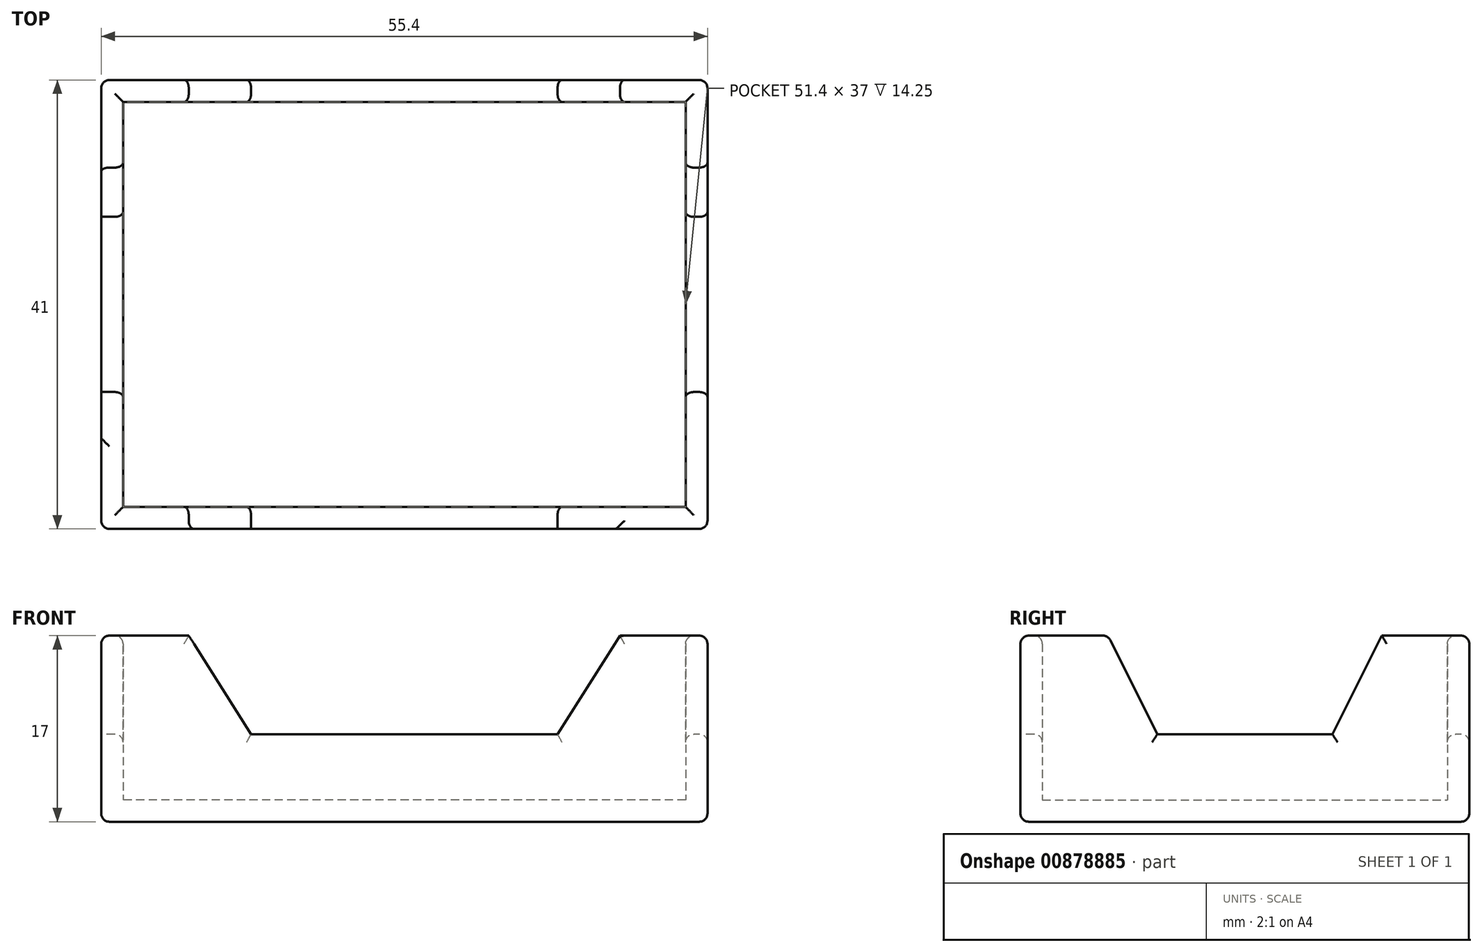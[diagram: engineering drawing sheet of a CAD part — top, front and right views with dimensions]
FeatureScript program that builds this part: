
annotation { "Feature Type Name" : "Feature", "Feature Type Description" : "" }
export const myFeature = defineFeature(function(context is Context, id is Id, definition is map)
    precondition{}
    {
        {
            var Q0;
            Q0=qCreatedBy(makeId("Top.planeOp"),FACE);
            var sketch = newSketch(context, id + "F0", { "sketchPlane" : qUnion([Q0])});
            skLineSegment(sketch, "E0.bottom", {"start": v(25.7, -18.5) * mm, "end": v(-25.7, -18.5) * mm});
            skLineSegment(sketch, "E0.top", {"start": v(25.7, 18.5) * mm, "end": v(-25.7, 18.5) * mm});
            skLineSegment(sketch, "E0.left", {"start": v(25.7, -18.5) * mm, "end": v(25.7, 18.5) * mm});
            skLineSegment(sketch, "E0.right", {"start": v(-25.7, -18.5) * mm, "end": v(-25.7, 18.5) * mm});
            skPoint(sketch, "E0.middle", {"position": v(0, 0) * mm});
            skLineSegment(sketch, "E1.0", {"start": v(27.7, 20.5) * mm, "end": v(-27.7, 20.5) * mm});
            skLineSegment(sketch, "E1.1", {"start": v(27.7, -20.5) * mm, "end": v(27.7, 20.5) * mm});
            skLineSegment(sketch, "E1.2", {"start": v(27.7, -20.5) * mm, "end": v(-27.7, -20.5) * mm});
            skLineSegment(sketch, "E1.3", {"start": v(-27.7, -20.5) * mm, "end": v(-27.7, 20.5) * mm});
            skSolve(sketch);
        }
        {
            var Q0;
            Q0=makeQuery(id+"F0.imprint","IMPRINT",FACE,{"disambiguationData":[TD([[makeQuery(id+"F0.imprint","IMPRINT",EDGE,{"derivedFrom":sQuery(id+"F0.wireOp",EDGE,"E0.bottom")}),1.0]])]});
            extrude(context, id + "F1", {"entities" : qUnion([Q0]), "depth" : 15 * mm, "offsetDistance" : 25 * mm});
        }
        {
            var Q0;
            Q0=makeQuery(id+"F0.imprint","IMPRINT",FACE,{"disambiguationData":[TD([[makeQuery(id+"F0.imprint","IMPRINT",EDGE,{"derivedFrom":sQuery(id+"F0.wireOp",EDGE,"E0.bottom")}),-1.0]])]});
            var Q1;
            Q1=makeQuery(id+"F0.imprint","IMPRINT",FACE,{"disambiguationData":[TD([[makeQuery(id+"F0.imprint","IMPRINT",EDGE,{"derivedFrom":sQuery(id+"F0.wireOp",EDGE,"E0.bottom")}),1.0]])]});
            extrude(context, id + "F2", {"entities" : qUnion([Q0, Q1]), "operationType" : NewBodyOperationType.ADD, "oppositeDirection" : true, "depth" : 2 * mm, "offsetDistance" : 25 * mm});
        }
        {
            var Q0;
            {var subQ0=sQuery(id+"F0.wireOp",EDGE,"E1.2");Q0=makeQuery(id+"F2.boolean.opBoolean","MERGE",FACE,{"derivedFrom":[makeQuery(id+"F1.opExtrude","SWEPT_FACE",FACE,{"disambiguationData":[OSD([subQ0])]}),makeQuery(id+"F2.opExtrude","SWEPT_FACE",FACE,{"disambiguationData":[OSD([subQ0])]})]});}
            var sketch = newSketch(context, id + "F3", { "sketchPlane" : qUnion([Q0])});
            skLineSegment(sketch, "E2", {"start": v(-19.7, 15) * mm, "end": v(-14, 6) * mm});
            skLineSegment(sketch, "E3", {"start": v(-14, 6) * mm, "end": v(14, 6) * mm});
            skLineSegment(sketch, "E4", {"start": v(14, 6) * mm, "end": v(19.7, 15) * mm});
            skSolve(sketch);
        }
        {
            var Q0;
            {var subQ0=sQuery(id+"F3.wireOp",EDGE,"E2");Q0=makeQuery(id+"F3.imprint","IMPRINT",FACE,{"disambiguationData":[TD([[makeQuery(id+"F3.imprint","IMPRINT",EDGE,{"derivedFrom":subQ0}),1.0]])]});}
            extrude(context, id + "F4", {"entities" : qUnion([Q0]), "operationType" : NewBodyOperationType.REMOVE, "endBound" : BoundingType.THROUGH_ALL, "oppositeDirection" : true, "depth" : 25 * mm, "offsetDistance" : 25 * mm});
        }
        {
            var Q0;
            {var subQ0=sQuery(id+"F0.wireOp",EDGE,"E1.3");Q0=makeQuery(id+"F2.boolean.opBoolean","MERGE",FACE,{"derivedFrom":[makeQuery(id+"F1.opExtrude","SWEPT_FACE",FACE,{"disambiguationData":[OSD([subQ0])]}),makeQuery(id+"F2.opExtrude","SWEPT_FACE",FACE,{"disambiguationData":[OSD([subQ0])]})]});}
            var sketch = newSketch(context, id + "F5", { "sketchPlane" : qUnion([Q0])});
            skLineSegment(sketch, "E5", {"start": v(-12.5, 15) * mm, "end": v(-8, 6) * mm});
            skLineSegment(sketch, "E6", {"start": v(-8, 6) * mm, "end": v(8, 6) * mm});
            skLineSegment(sketch, "E7", {"start": v(8, 6) * mm, "end": v(12.5, 15) * mm});
            skSolve(sketch);
        }
        {
            var Q0;
            {var subQ0=sQuery(id+"F5.wireOp",EDGE,"E5");Q0=makeQuery(id+"F5.imprint","IMPRINT",FACE,{"disambiguationData":[TD([[makeQuery(id+"F5.imprint","IMPRINT",EDGE,{"derivedFrom":subQ0}),1.0]])]});}
            extrude(context, id + "F6", {"entities" : qUnion([Q0]), "operationType" : NewBodyOperationType.REMOVE, "endBound" : BoundingType.THROUGH_ALL, "oppositeDirection" : true, "depth" : 25 * mm, "offsetDistance" : 25 * mm});
        }
        {
            var Q0;
            {var subQ0=sQuery(id+"F0.wireOp",EDGE,"E1.0");Q0=makeQuery(id+"F4.boolean.opBoolean","INTERSECT",EDGE,{"derivedFrom":[makeQuery(id+"F2.boolean.opBoolean","MERGE",FACE,{"derivedFrom":[makeQuery(id+"F1.opExtrude","SWEPT_FACE",FACE,{"disambiguationData":[OSD([subQ0])]}),makeQuery(id+"F2.opExtrude","SWEPT_FACE",FACE,{"disambiguationData":[OSD([subQ0])]})]}),makeQuery(id+"F4.opExtrude","SWEPT_FACE",FACE,{"disambiguationData":[OSD([sQuery(id+"F3.wireOp",EDGE,"E3")])]})]});}
            var Q1;
            {var subQ0=sQuery(id+"F0.wireOp",EDGE,"E1.0");Q1=makeQuery(id+"F4.boolean.opBoolean","INTERSECT",EDGE,{"derivedFrom":[makeQuery(id+"F2.boolean.opBoolean","MERGE",FACE,{"derivedFrom":[makeQuery(id+"F1.opExtrude","SWEPT_FACE",FACE,{"disambiguationData":[OSD([subQ0])]}),makeQuery(id+"F2.opExtrude","SWEPT_FACE",FACE,{"disambiguationData":[OSD([subQ0])]})]}),makeQuery(id+"F4.opExtrude","SWEPT_FACE",FACE,{"disambiguationData":[OSD([sQuery(id+"F3.wireOp",EDGE,"E4")])]})]});}
            var Q2;
            {var subQ0=sQuery(id+"F0.wireOp",EDGE,"E1.0");var subQ1=sQuery(id+"F0.wireOp",EDGE,"E1.1");Q2=makeQuery(id+"F4.boolean.opBoolean","SPLIT",EDGE,{"disambiguationData":[TD([makeQuery(id+"F1.opExtrude","SWEPT_FACE",FACE,{"disambiguationData":[OSD([subQ1])]})])],"derivedFrom":makeQuery(id+"F1.opExtrude","CAP_EDGE",EDGE,{"disambiguationData":[OSD([subQ0])],"isStart":false})});}
            var Q3;
            {var subQ0=sQuery(id+"F0.wireOp",EDGE,"E1.0");var subQ1=sQuery(id+"F0.wireOp",EDGE,"E1.1");Q3=makeQuery(id+"F6.boolean.opBoolean","SPLIT",EDGE,{"disambiguationData":[TD([makeQuery(id+"F1.opExtrude","SWEPT_FACE",FACE,{"disambiguationData":[OSD([subQ0])]})])],"derivedFrom":makeQuery(id+"F1.opExtrude","CAP_EDGE",EDGE,{"disambiguationData":[OSD([subQ1])],"isStart":false})});}
            var Q4;
            {var subQ0=sQuery(id+"F0.wireOp",EDGE,"E1.1");var subQ1=sQuery(id+"F0.wireOp",EDGE,"E1.0");Q4=makeQuery(id+"F2.boolean.opBoolean","MERGE",EDGE,{"derivedFrom":[makeQuery(id+"F1.opExtrude","SWEPT_EDGE",EDGE,{"disambiguationData":[OSD([subQ1,subQ0])]}),makeQuery(id+"F2.opExtrude","SWEPT_EDGE",EDGE,{"disambiguationData":[OSD([subQ1,subQ0])]})]});}
            var Q5;
            {var subQ0=sQuery(id+"F0.wireOp",EDGE,"E1.0");Q5=makeQuery(id+"F4.boolean.opBoolean","INTERSECT",EDGE,{"derivedFrom":[makeQuery(id+"F2.boolean.opBoolean","MERGE",FACE,{"derivedFrom":[makeQuery(id+"F1.opExtrude","SWEPT_FACE",FACE,{"disambiguationData":[OSD([subQ0])]}),makeQuery(id+"F2.opExtrude","SWEPT_FACE",FACE,{"disambiguationData":[OSD([subQ0])]})]}),makeQuery(id+"F4.opExtrude","SWEPT_FACE",FACE,{"disambiguationData":[OSD([sQuery(id+"F3.wireOp",EDGE,"E2")])]})]});}
            var Q6;
            {var subQ0=sQuery(id+"F0.wireOp",EDGE,"E1.3");var subQ1=sQuery(id+"F0.wireOp",EDGE,"E1.0");Q6=makeQuery(id+"F4.boolean.opBoolean","SPLIT",EDGE,{"disambiguationData":[TD([makeQuery(id+"F1.opExtrude","SWEPT_FACE",FACE,{"disambiguationData":[OSD([subQ0])]})])],"derivedFrom":makeQuery(id+"F1.opExtrude","CAP_EDGE",EDGE,{"disambiguationData":[OSD([subQ1])],"isStart":false})});}
            var Q7;
            {var subQ0=sQuery(id+"F0.wireOp",EDGE,"E1.3");var subQ1=sQuery(id+"F0.wireOp",EDGE,"E1.0");Q7=makeQuery(id+"F2.boolean.opBoolean","MERGE",EDGE,{"derivedFrom":[makeQuery(id+"F1.opExtrude","SWEPT_EDGE",EDGE,{"disambiguationData":[OSD([subQ1,subQ0])]}),makeQuery(id+"F2.opExtrude","SWEPT_EDGE",EDGE,{"disambiguationData":[OSD([subQ1,subQ0])]})]});}
            var Q8;
            {var subQ0=sQuery(id+"F0.wireOp",EDGE,"E1.3");var subQ1=sQuery(id+"F0.wireOp",EDGE,"E1.0");Q8=makeQuery(id+"F6.boolean.opBoolean","SPLIT",EDGE,{"disambiguationData":[TD([makeQuery(id+"F1.opExtrude","SWEPT_FACE",FACE,{"disambiguationData":[OSD([subQ1])]})])],"derivedFrom":makeQuery(id+"F1.opExtrude","CAP_EDGE",EDGE,{"disambiguationData":[OSD([subQ0])],"isStart":false})});}
            var Q9;
            {var subQ0=sQuery(id+"F0.wireOp",EDGE,"E0.right");var subQ1=sQuery(id+"F0.wireOp",EDGE,"E0.top");Q9=makeQuery(id+"F6.boolean.opBoolean","SPLIT",EDGE,{"disambiguationData":[TD([makeQuery(id+"F1.opExtrude","SWEPT_FACE",FACE,{"disambiguationData":[OSD([subQ1])]})])],"derivedFrom":makeQuery(id+"F1.opExtrude","CAP_EDGE",EDGE,{"disambiguationData":[OSD([subQ0])],"isStart":false})});}
            var Q10;
            {var subQ0=sQuery(id+"F0.wireOp",EDGE,"E0.right");var subQ1=sQuery(id+"F0.wireOp",EDGE,"E0.top");Q10=makeQuery(id+"F4.boolean.opBoolean","SPLIT",EDGE,{"disambiguationData":[TD([makeQuery(id+"F1.opExtrude","SWEPT_FACE",FACE,{"disambiguationData":[OSD([subQ0])]})])],"derivedFrom":makeQuery(id+"F1.opExtrude","CAP_EDGE",EDGE,{"disambiguationData":[OSD([subQ1])],"isStart":false})});}
            var Q11;
            Q11=makeQuery(id+"F4.boolean.opBoolean","INTERSECT",EDGE,{"derivedFrom":[makeQuery(id+"F1.opExtrude","SWEPT_FACE",FACE,{"disambiguationData":[OSD([sQuery(id+"F0.wireOp",EDGE,"E0.top")])]}),makeQuery(id+"F4.opExtrude","SWEPT_FACE",FACE,{"disambiguationData":[OSD([sQuery(id+"F3.wireOp",EDGE,"E2")])]})]});
            var Q12;
            Q12=makeQuery(id+"F4.boolean.opBoolean","INTERSECT",EDGE,{"derivedFrom":[makeQuery(id+"F1.opExtrude","SWEPT_FACE",FACE,{"disambiguationData":[OSD([sQuery(id+"F0.wireOp",EDGE,"E0.top")])]}),makeQuery(id+"F4.opExtrude","SWEPT_FACE",FACE,{"disambiguationData":[OSD([sQuery(id+"F3.wireOp",EDGE,"E3")])]})]});
            var Q13;
            Q13=makeQuery(id+"F4.boolean.opBoolean","INTERSECT",EDGE,{"derivedFrom":[makeQuery(id+"F1.opExtrude","SWEPT_FACE",FACE,{"disambiguationData":[OSD([sQuery(id+"F0.wireOp",EDGE,"E0.top")])]}),makeQuery(id+"F4.opExtrude","SWEPT_FACE",FACE,{"disambiguationData":[OSD([sQuery(id+"F3.wireOp",EDGE,"E4")])]})]});
            var Q14;
            {var subQ0=sQuery(id+"F0.wireOp",EDGE,"E0.left");var subQ1=sQuery(id+"F0.wireOp",EDGE,"E0.top");Q14=makeQuery(id+"F4.boolean.opBoolean","SPLIT",EDGE,{"disambiguationData":[TD([makeQuery(id+"F1.opExtrude","SWEPT_FACE",FACE,{"disambiguationData":[OSD([subQ0])]})])],"derivedFrom":makeQuery(id+"F1.opExtrude","CAP_EDGE",EDGE,{"disambiguationData":[OSD([subQ1])],"isStart":false})});}
            var Q15;
            {var subQ0=sQuery(id+"F0.wireOp",EDGE,"E0.left");var subQ1=sQuery(id+"F0.wireOp",EDGE,"E0.top");Q15=makeQuery(id+"F6.boolean.opBoolean","SPLIT",EDGE,{"disambiguationData":[TD([makeQuery(id+"F1.opExtrude","SWEPT_FACE",FACE,{"disambiguationData":[OSD([subQ1])]})])],"derivedFrom":makeQuery(id+"F1.opExtrude","CAP_EDGE",EDGE,{"disambiguationData":[OSD([subQ0])],"isStart":false})});}
            var Q16;
            {var subQ1=sQuery(id+"F0.wireOp",EDGE,"E0.left");var subQ2=sQuery(id+"F0.wireOp",EDGE,"E1.3");var subQ3=sQuery(id+"F5.wireOp",EDGE,"E5");Q16=makeQuery(id+"F6.boolean.opBoolean","COPY",EDGE,{"disambiguationData":[TD([makeQuery(id+"F1.opExtrude","SWEPT_FACE",FACE,{"disambiguationData":[OSD([subQ1])]})])],"derivedFrom":makeQuery(id+"F6.opExtrude","SWEPT_EDGE",EDGE,{"disambiguationData":[OSD([subQ2,subQ3])]})});}
            var Q17;
            {var subQ0=sQuery(id+"F0.wireOp",EDGE,"E1.1");Q17=makeQuery(id+"F6.boolean.opBoolean","INTERSECT",EDGE,{"derivedFrom":[makeQuery(id+"F2.boolean.opBoolean","MERGE",FACE,{"derivedFrom":[makeQuery(id+"F1.opExtrude","SWEPT_FACE",FACE,{"disambiguationData":[OSD([subQ0])]}),makeQuery(id+"F2.opExtrude","SWEPT_FACE",FACE,{"disambiguationData":[OSD([subQ0])]})]}),makeQuery(id+"F6.opExtrude","SWEPT_FACE",FACE,{"disambiguationData":[OSD([sQuery(id+"F5.wireOp",EDGE,"E5")])]})]});}
            var Q18;
            Q18=makeQuery(id+"F6.boolean.opBoolean","INTERSECT",EDGE,{"derivedFrom":[makeQuery(id+"F1.opExtrude","SWEPT_FACE",FACE,{"disambiguationData":[OSD([sQuery(id+"F0.wireOp",EDGE,"E0.left")])]}),makeQuery(id+"F6.opExtrude","SWEPT_FACE",FACE,{"disambiguationData":[OSD([sQuery(id+"F5.wireOp",EDGE,"E5")])]})]});
            var Q19;
            Q19=makeQuery(id+"F6.boolean.opBoolean","INTERSECT",EDGE,{"derivedFrom":[makeQuery(id+"F1.opExtrude","SWEPT_FACE",FACE,{"disambiguationData":[OSD([sQuery(id+"F0.wireOp",EDGE,"E0.left")])]}),makeQuery(id+"F6.opExtrude","SWEPT_FACE",FACE,{"disambiguationData":[OSD([sQuery(id+"F5.wireOp",EDGE,"E6")])]})]});
            var Q20;
            {var subQ0=sQuery(id+"F0.wireOp",EDGE,"E1.1");Q20=makeQuery(id+"F6.boolean.opBoolean","INTERSECT",EDGE,{"derivedFrom":[makeQuery(id+"F2.boolean.opBoolean","MERGE",FACE,{"derivedFrom":[makeQuery(id+"F1.opExtrude","SWEPT_FACE",FACE,{"disambiguationData":[OSD([subQ0])]}),makeQuery(id+"F2.opExtrude","SWEPT_FACE",FACE,{"disambiguationData":[OSD([subQ0])]})]}),makeQuery(id+"F6.opExtrude","SWEPT_FACE",FACE,{"disambiguationData":[OSD([sQuery(id+"F5.wireOp",EDGE,"E6")])]})]});}
            var Q21;
            {var subQ0=sQuery(id+"F0.wireOp",EDGE,"E1.1");Q21=makeQuery(id+"F6.boolean.opBoolean","INTERSECT",EDGE,{"derivedFrom":[makeQuery(id+"F2.boolean.opBoolean","MERGE",FACE,{"derivedFrom":[makeQuery(id+"F1.opExtrude","SWEPT_FACE",FACE,{"disambiguationData":[OSD([subQ0])]}),makeQuery(id+"F2.opExtrude","SWEPT_FACE",FACE,{"disambiguationData":[OSD([subQ0])]})]}),makeQuery(id+"F6.opExtrude","SWEPT_FACE",FACE,{"disambiguationData":[OSD([sQuery(id+"F5.wireOp",EDGE,"E7")])]})]});}
            var Q22;
            Q22=makeQuery(id+"F6.boolean.opBoolean","INTERSECT",EDGE,{"derivedFrom":[makeQuery(id+"F1.opExtrude","SWEPT_FACE",FACE,{"disambiguationData":[OSD([sQuery(id+"F0.wireOp",EDGE,"E0.left")])]}),makeQuery(id+"F6.opExtrude","SWEPT_FACE",FACE,{"disambiguationData":[OSD([sQuery(id+"F5.wireOp",EDGE,"E7")])]})]});
            var Q23;
            {var subQ1=sQuery(id+"F5.wireOp",EDGE,"E7");var subQ2=sQuery(id+"F0.wireOp",EDGE,"E0.left");var subQ3=sQuery(id+"F0.wireOp",EDGE,"E1.3");Q23=makeQuery(id+"F6.boolean.opBoolean","COPY",EDGE,{"disambiguationData":[TD([makeQuery(id+"F1.opExtrude","SWEPT_FACE",FACE,{"disambiguationData":[OSD([subQ2])]})])],"derivedFrom":makeQuery(id+"F6.opExtrude","SWEPT_EDGE",EDGE,{"disambiguationData":[OSD([subQ3,subQ1])]})});}
            var Q24;
            {var subQ0=sQuery(id+"F0.wireOp",EDGE,"E1.1");var subQ1=sQuery(id+"F0.wireOp",EDGE,"E1.2");Q24=makeQuery(id+"F6.boolean.opBoolean","SPLIT",EDGE,{"disambiguationData":[TD([makeQuery(id+"F1.opExtrude","SWEPT_FACE",FACE,{"disambiguationData":[OSD([subQ1])]})])],"derivedFrom":makeQuery(id+"F1.opExtrude","CAP_EDGE",EDGE,{"disambiguationData":[OSD([subQ0])],"isStart":false})});}
            var Q25;
            {var subQ0=sQuery(id+"F0.wireOp",EDGE,"E0.bottom");var subQ1=sQuery(id+"F0.wireOp",EDGE,"E0.left");Q25=makeQuery(id+"F6.boolean.opBoolean","SPLIT",EDGE,{"disambiguationData":[TD([makeQuery(id+"F1.opExtrude","SWEPT_FACE",FACE,{"disambiguationData":[OSD([subQ0])]})])],"derivedFrom":makeQuery(id+"F1.opExtrude","CAP_EDGE",EDGE,{"disambiguationData":[OSD([subQ1])],"isStart":false})});}
            var Q26;
            {var subQ0=sQuery(id+"F0.wireOp",EDGE,"E0.bottom");var subQ1=sQuery(id+"F0.wireOp",EDGE,"E0.left");Q26=makeQuery(id+"F4.boolean.opBoolean","SPLIT",EDGE,{"disambiguationData":[TD([makeQuery(id+"F1.opExtrude","SWEPT_FACE",FACE,{"disambiguationData":[OSD([subQ1])]})])],"derivedFrom":makeQuery(id+"F1.opExtrude","CAP_EDGE",EDGE,{"disambiguationData":[OSD([subQ0])],"isStart":false})});}
            var Q27;
            {var subQ0=sQuery(id+"F0.wireOp",EDGE,"E1.1");var subQ1=sQuery(id+"F0.wireOp",EDGE,"E1.2");Q27=makeQuery(id+"F4.boolean.opBoolean","SPLIT",EDGE,{"disambiguationData":[TD([makeQuery(id+"F1.opExtrude","SWEPT_FACE",FACE,{"disambiguationData":[OSD([subQ0])]})])],"derivedFrom":makeQuery(id+"F1.opExtrude","CAP_EDGE",EDGE,{"disambiguationData":[OSD([subQ1])],"isStart":false})});}
            var Q28;
            {var subQ0=sQuery(id+"F0.wireOp",EDGE,"E1.2");var subQ1=sQuery(id+"F0.wireOp",EDGE,"E1.1");Q28=makeQuery(id+"F2.boolean.opBoolean","MERGE",EDGE,{"derivedFrom":[makeQuery(id+"F1.opExtrude","SWEPT_EDGE",EDGE,{"disambiguationData":[OSD([subQ1,subQ0])]}),makeQuery(id+"F2.opExtrude","SWEPT_EDGE",EDGE,{"disambiguationData":[OSD([subQ1,subQ0])]})]});}
            var Q29;
            {var subQ0=sQuery(id+"F0.wireOp",EDGE,"E1.2");var subQ1=sQuery(id+"F0.wireOp",EDGE,"E0.bottom");var subQ2=sQuery(id+"F3.wireOp",EDGE,"E4");Q29=makeQuery(id+"F4.boolean.opBoolean","COPY",EDGE,{"disambiguationData":[TD([makeQuery(id+"F1.opExtrude","SWEPT_FACE",FACE,{"disambiguationData":[OSD([subQ1])]})])],"derivedFrom":makeQuery(id+"F4.opExtrude","SWEPT_EDGE",EDGE,{"disambiguationData":[OSD([subQ0,subQ2])]})});}
            var Q30;
            Q30=makeQuery(id+"F4.boolean.opBoolean","INTERSECT",EDGE,{"derivedFrom":[makeQuery(id+"F1.opExtrude","SWEPT_FACE",FACE,{"disambiguationData":[OSD([sQuery(id+"F0.wireOp",EDGE,"E0.bottom")])]}),makeQuery(id+"F4.opExtrude","SWEPT_FACE",FACE,{"disambiguationData":[OSD([sQuery(id+"F3.wireOp",EDGE,"E4")])]})]});
            var Q31;
            Q31=makeQuery(id+"F4.boolean.opBoolean","COPY",EDGE,{"derivedFrom":makeQuery(id+"F4.opExtrude","CAP_EDGE",EDGE,{"disambiguationData":[OSD([sQuery(id+"F3.wireOp",EDGE,"E4")])],"isStart":true})});
            var Q32;
            Q32=makeQuery(id+"F4.boolean.opBoolean","COPY",EDGE,{"derivedFrom":makeQuery(id+"F4.opExtrude","CAP_EDGE",EDGE,{"disambiguationData":[OSD([sQuery(id+"F3.wireOp",EDGE,"E3")])],"isStart":true})});
            var Q33;
            Q33=makeQuery(id+"F4.boolean.opBoolean","INTERSECT",EDGE,{"derivedFrom":[makeQuery(id+"F1.opExtrude","SWEPT_FACE",FACE,{"disambiguationData":[OSD([sQuery(id+"F0.wireOp",EDGE,"E0.bottom")])]}),makeQuery(id+"F4.opExtrude","SWEPT_FACE",FACE,{"disambiguationData":[OSD([sQuery(id+"F3.wireOp",EDGE,"E3")])]})]});
            var Q34;
            Q34=makeQuery(id+"F4.boolean.opBoolean","INTERSECT",EDGE,{"derivedFrom":[makeQuery(id+"F1.opExtrude","SWEPT_FACE",FACE,{"disambiguationData":[OSD([sQuery(id+"F0.wireOp",EDGE,"E0.bottom")])]}),makeQuery(id+"F4.opExtrude","SWEPT_FACE",FACE,{"disambiguationData":[OSD([sQuery(id+"F3.wireOp",EDGE,"E2")])]})]});
            var Q35;
            Q35=makeQuery(id+"F4.boolean.opBoolean","COPY",EDGE,{"derivedFrom":makeQuery(id+"F4.opExtrude","CAP_EDGE",EDGE,{"disambiguationData":[OSD([sQuery(id+"F3.wireOp",EDGE,"E2")])],"isStart":true})});
            var Q36;
            {var subQ0=sQuery(id+"F0.wireOp",EDGE,"E1.2");var subQ1=sQuery(id+"F0.wireOp",EDGE,"E0.bottom");var subQ2=sQuery(id+"F3.wireOp",EDGE,"E2");Q36=makeQuery(id+"F4.boolean.opBoolean","COPY",EDGE,{"disambiguationData":[TD([makeQuery(id+"F1.opExtrude","SWEPT_FACE",FACE,{"disambiguationData":[OSD([subQ1])]})])],"derivedFrom":makeQuery(id+"F4.opExtrude","SWEPT_EDGE",EDGE,{"disambiguationData":[OSD([subQ0,subQ2])]})});}
            var Q37;
            {var subQ0=sQuery(id+"F0.wireOp",EDGE,"E0.bottom");var subQ1=sQuery(id+"F0.wireOp",EDGE,"E0.right");Q37=makeQuery(id+"F4.boolean.opBoolean","SPLIT",EDGE,{"disambiguationData":[TD([makeQuery(id+"F1.opExtrude","SWEPT_FACE",FACE,{"disambiguationData":[OSD([subQ1])]})])],"derivedFrom":makeQuery(id+"F1.opExtrude","CAP_EDGE",EDGE,{"disambiguationData":[OSD([subQ0])],"isStart":false})});}
            var Q38;
            {var subQ0=sQuery(id+"F0.wireOp",EDGE,"E1.2");var subQ1=sQuery(id+"F0.wireOp",EDGE,"E1.3");Q38=makeQuery(id+"F4.boolean.opBoolean","SPLIT",EDGE,{"disambiguationData":[TD([makeQuery(id+"F1.opExtrude","SWEPT_FACE",FACE,{"disambiguationData":[OSD([subQ1])]})])],"derivedFrom":makeQuery(id+"F1.opExtrude","CAP_EDGE",EDGE,{"disambiguationData":[OSD([subQ0])],"isStart":false})});}
            var Q39;
            {var subQ0=sQuery(id+"F0.wireOp",EDGE,"E0.bottom");var subQ1=sQuery(id+"F0.wireOp",EDGE,"E0.right");Q39=makeQuery(id+"F6.boolean.opBoolean","SPLIT",EDGE,{"disambiguationData":[TD([makeQuery(id+"F1.opExtrude","SWEPT_FACE",FACE,{"disambiguationData":[OSD([subQ0])]})])],"derivedFrom":makeQuery(id+"F1.opExtrude","CAP_EDGE",EDGE,{"disambiguationData":[OSD([subQ1])],"isStart":false})});}
            var Q40;
            {var subQ0=sQuery(id+"F0.wireOp",EDGE,"E1.3");var subQ1=sQuery(id+"F0.wireOp",EDGE,"E0.right");var subQ2=sQuery(id+"F5.wireOp",EDGE,"E7");Q40=makeQuery(id+"F6.boolean.opBoolean","COPY",EDGE,{"disambiguationData":[TD([makeQuery(id+"F1.opExtrude","SWEPT_FACE",FACE,{"disambiguationData":[OSD([subQ1])]})])],"derivedFrom":makeQuery(id+"F6.opExtrude","SWEPT_EDGE",EDGE,{"disambiguationData":[OSD([subQ0,subQ2])]})});}
            var Q41;
            {var subQ0=sQuery(id+"F0.wireOp",EDGE,"E1.2");var subQ1=sQuery(id+"F0.wireOp",EDGE,"E1.3");Q41=makeQuery(id+"F6.boolean.opBoolean","SPLIT",EDGE,{"disambiguationData":[TD([makeQuery(id+"F1.opExtrude","SWEPT_FACE",FACE,{"disambiguationData":[OSD([subQ0])]})])],"derivedFrom":makeQuery(id+"F1.opExtrude","CAP_EDGE",EDGE,{"disambiguationData":[OSD([subQ1])],"isStart":false})});}
            var Q42;
            Q42=makeQuery(id+"F6.boolean.opBoolean","INTERSECT",EDGE,{"derivedFrom":[makeQuery(id+"F1.opExtrude","SWEPT_FACE",FACE,{"disambiguationData":[OSD([sQuery(id+"F0.wireOp",EDGE,"E0.right")])]}),makeQuery(id+"F6.opExtrude","SWEPT_FACE",FACE,{"disambiguationData":[OSD([sQuery(id+"F5.wireOp",EDGE,"E7")])]})]});
            var Q43;
            Q43=makeQuery(id+"F6.boolean.opBoolean","COPY",EDGE,{"derivedFrom":makeQuery(id+"F6.opExtrude","CAP_EDGE",EDGE,{"disambiguationData":[OSD([sQuery(id+"F5.wireOp",EDGE,"E7")])],"isStart":true})});
            var Q44;
            {var subQ0=sQuery(id+"F0.wireOp",EDGE,"E1.3");var subQ1=sQuery(id+"F0.wireOp",EDGE,"E0.right");var subQ2=sQuery(id+"F5.wireOp",EDGE,"E5");Q44=makeQuery(id+"F6.boolean.opBoolean","COPY",EDGE,{"disambiguationData":[TD([makeQuery(id+"F1.opExtrude","SWEPT_FACE",FACE,{"disambiguationData":[OSD([subQ1])]})])],"derivedFrom":makeQuery(id+"F6.opExtrude","SWEPT_EDGE",EDGE,{"disambiguationData":[OSD([subQ0,subQ2])]})});}
            var Q45;
            Q45=makeQuery(id+"F6.boolean.opBoolean","COPY",EDGE,{"derivedFrom":makeQuery(id+"F6.opExtrude","CAP_EDGE",EDGE,{"disambiguationData":[OSD([sQuery(id+"F5.wireOp",EDGE,"E6")])],"isStart":true})});
            var Q46;
            Q46=makeQuery(id+"F6.boolean.opBoolean","INTERSECT",EDGE,{"derivedFrom":[makeQuery(id+"F1.opExtrude","SWEPT_FACE",FACE,{"disambiguationData":[OSD([sQuery(id+"F0.wireOp",EDGE,"E0.right")])]}),makeQuery(id+"F6.opExtrude","SWEPT_FACE",FACE,{"disambiguationData":[OSD([sQuery(id+"F5.wireOp",EDGE,"E6")])]})]});
            var Q47;
            Q47=makeQuery(id+"F6.boolean.opBoolean","INTERSECT",EDGE,{"derivedFrom":[makeQuery(id+"F1.opExtrude","SWEPT_FACE",FACE,{"disambiguationData":[OSD([sQuery(id+"F0.wireOp",EDGE,"E0.right")])]}),makeQuery(id+"F6.opExtrude","SWEPT_FACE",FACE,{"disambiguationData":[OSD([sQuery(id+"F5.wireOp",EDGE,"E5")])]})]});
            var Q48;
            Q48=makeQuery(id+"F6.boolean.opBoolean","COPY",EDGE,{"derivedFrom":makeQuery(id+"F6.opExtrude","CAP_EDGE",EDGE,{"disambiguationData":[OSD([sQuery(id+"F5.wireOp",EDGE,"E5")])],"isStart":true})});
            var Q49;
            {var subQ0=sQuery(id+"F0.wireOp",EDGE,"E1.3");var subQ1=sQuery(id+"F0.wireOp",EDGE,"E1.2");Q49=makeQuery(id+"F2.boolean.opBoolean","MERGE",EDGE,{"derivedFrom":[makeQuery(id+"F1.opExtrude","SWEPT_EDGE",EDGE,{"disambiguationData":[OSD([subQ1,subQ0])]}),makeQuery(id+"F2.opExtrude","SWEPT_EDGE",EDGE,{"disambiguationData":[OSD([subQ1,subQ0])]})]});}
            var Q50;
            Q50=makeQuery(id+"F2.opExtrude","CAP_EDGE",EDGE,{"disambiguationData":[OSD([sQuery(id+"F0.wireOp",EDGE,"E1.3")])],"isStart":false});
            var Q51;
            Q51=makeQuery(id+"F2.opExtrude","CAP_EDGE",EDGE,{"disambiguationData":[OSD([sQuery(id+"F0.wireOp",EDGE,"E1.0")])],"isStart":false});
            var Q52;
            Q52=makeQuery(id+"F2.opExtrude","CAP_EDGE",EDGE,{"disambiguationData":[OSD([sQuery(id+"F0.wireOp",EDGE,"E1.2")])],"isStart":false});
            var Q53;
            Q53=makeQuery(id+"F2.opExtrude","CAP_EDGE",EDGE,{"disambiguationData":[OSD([sQuery(id+"F0.wireOp",EDGE,"E1.1")])],"isStart":false});
            fillet(context, id + "F7", {"entities" : qUnion([Q0, Q1, Q2, Q3, Q4, Q5, Q6, Q7, Q8, Q9, Q10, Q11, Q12, Q13, Q14, Q15, Q16, Q17, Q18, Q19, Q20, Q21, Q22, Q23, Q24, Q25, Q26, Q27, Q28, Q29, Q30, Q31, Q32, Q33, Q34, Q35, Q36, Q37, Q38, Q39, Q40, Q41, Q42, Q43, Q44, Q45, Q46, Q47, Q48, Q49, Q50, Q51, Q52, Q53]), "tangentPropagation" : true, "radius" : 0.75 * mm, "defaultsChanged" : false, "vertexSettings" : [], "allowEdgeOverflow" : false});
        }
    });
